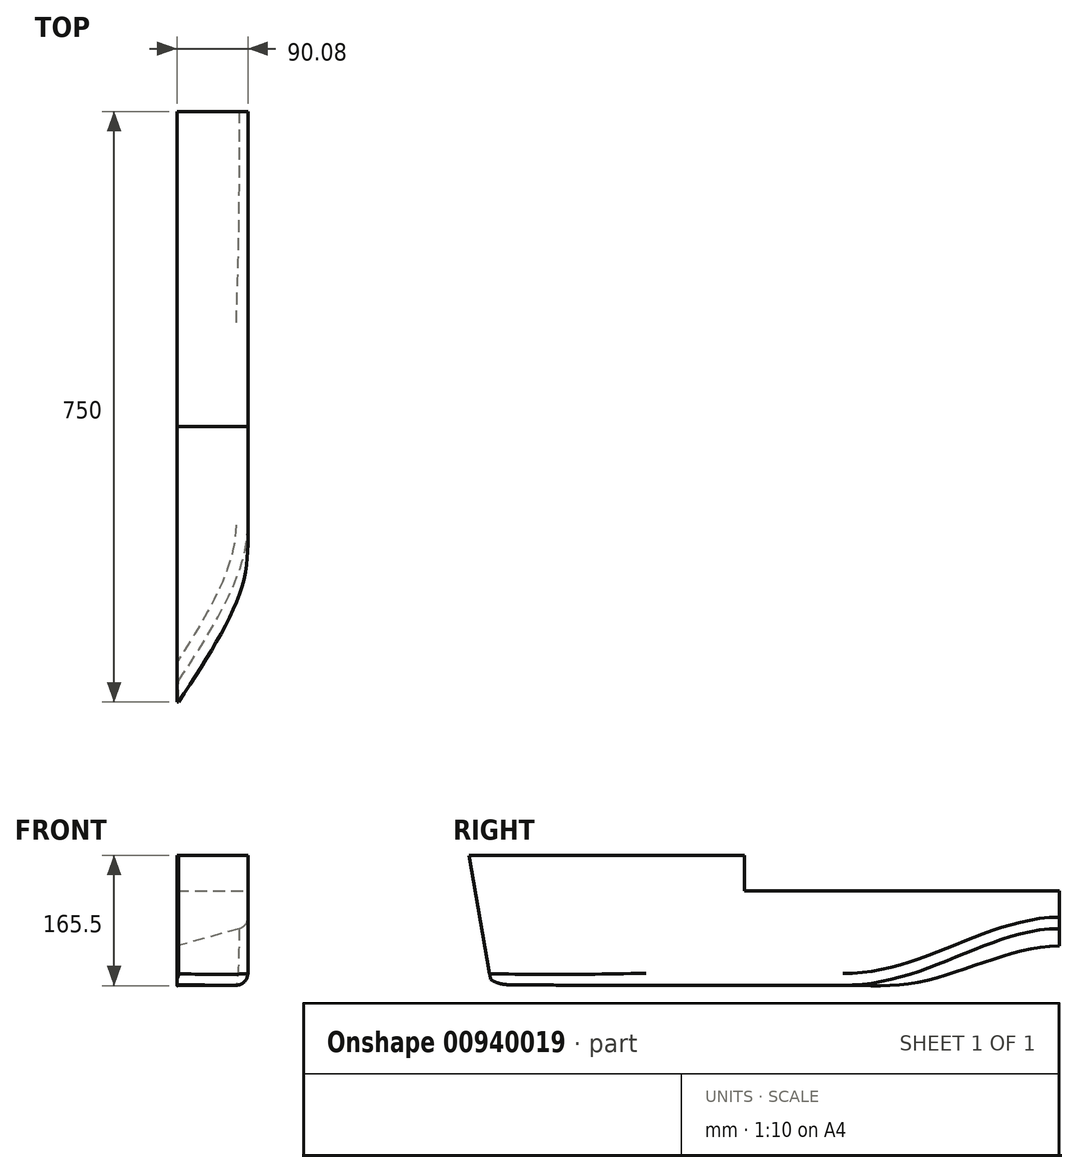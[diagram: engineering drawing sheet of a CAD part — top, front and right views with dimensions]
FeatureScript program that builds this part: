
annotation { "Feature Type Name" : "Feature", "Feature Type Description" : "" }
export const myFeature = defineFeature(function(context is Context, id is Id, definition is map)
    precondition{}
    {
        {
            var Q0;
            Q0=qCreatedBy(makeId("Front.planeOp"),FACE);
            var sketch = newSketch(context, id + "F0", { "sketchPlane" : qUnion([Q0])});
            skLineSegment(sketch, "E0", {"start": v(0, 0) * mm, "end": v(0, 90) * mm});
            skLineSegment(sketch, "E1", {"start": v(0, 90) * mm, "end": v(90, 90) * mm});
            skLineSegment(sketch, "E2", {"start": v(90, 90) * mm, "end": v(90, -75) * mm});
            skLineSegment(sketch, "E3", {"start": v(90, -75) * mm, "end": v(0, -75) * mm});
            skLineSegment(sketch, "E4", {"start": v(0, -75) * mm, "end": v(0, 0) * mm});
            skSolve(sketch);
        }
        {
            var Q0;
            Q0=makeQuery(id+"F0.imprint","IMPRINT",FACE,{"disambiguationData":[TD([[makeQuery(id+"F0.imprint","IMPRINT",EDGE,{"derivedFrom":sQuery(id+"F0.wireOp",EDGE,"E0")}),-1.0]])]});
            extrude(context, id + "F1", {"entities" : qUnion([Q0]), "depth" : 250 * mm, "offsetDistance" : 25 * mm, "symmetric" : true});
        }
        {
            var Q0;
            Q0=makeQuery(id+"F1.opExtrude","SWEPT_FACE",FACE,{"disambiguationData":[OSD([sQuery(id+"F0.wireOp",EDGE,"E0"),sQuery(id+"F0.wireOp",EDGE,"E4")])]});
            var sketch = newSketch(context, id + "F2", { "sketchPlane" : qUnion([Q0])});
            skLineSegment(sketch, "E5", {"start": v(0, 90) * mm, "end": v(350, 90) * mm});
            skLineSegment(sketch, "E6", {"start": v(0, 90) * mm, "end": v(-400, 90) * mm});
            skLineSegment(sketch, "E7", {"start": v(0, -75) * mm, "end": v(-400, -75) * mm});
            skLineSegment(sketch, "E8", {"start": v(0, -75) * mm, "end": v(350, -75) * mm});
            skSolve(sketch);
        }
        {
            var Q0;
            Q0=qCreatedBy(makeId("Front.planeOp"),FACE);
            cPlane(context, id + "F3", {"entities" : qUnion([Q0]), "cplaneType" : CPlaneType.OFFSET, "offset" : 350 * mm, "width" : 150 * mm, "height" : 150 * mm});
        }
        {
            var Q0;
            Q0=qCreatedBy(id+"F3.planeOp",FACE);
            var sketch = newSketch(context, id + "F4", { "sketchPlane" : qUnion([Q0])});
            skLineSegment(sketch, "E9", {"start": v(0, 90) * mm, "end": v(90, 90) * mm});
            skSolve(sketch);
        }
        {
            var Q0;
            Q0=sQuery(id+"F4.wireOp",EDGE,"E9");
            cPlane(context, id + "F5", {"entities" : qUnion([Q0]), "cplaneType" : CPlaneType.LINE_ANGLE, "offset" : 25 * mm, "angle" : 10 * degree, "width" : 150 * mm, "height" : 150 * mm});
        }
        {
            var Q0;
            Q0=qCreatedBy(id+"F5.planeOp",FACE);
            var sketch = newSketch(context, id + "F6", { "sketchPlane" : qUnion([Q0])});
            skLineSegment(sketch, "E10", {"start": v(0, 58.2) * mm, "end": v(0, 149.4) * mm});
            skLineSegment(sketch, "E11", {"start": v(0, 58.2) * mm, "end": v(0, -17.18) * mm});
            skLineSegment(sketch, "E12", {"start": v(0, 149.4) * mm, "end": v(-2, 149.4) * mm});
            skLineSegment(sketch, "E13", {"start": v(-2, 149.4) * mm, "end": v(-2, -17.18) * mm});
            skLineSegment(sketch, "E14", {"start": v(-2, -17.18) * mm, "end": v(0, -17.18) * mm});
            skSolve(sketch);
        }
        {
            var Q0;
            Q0=qCreatedBy(makeId("Front.planeOp"),FACE);
            cPlane(context, id + "F7", {"entities" : qUnion([Q0]), "cplaneType" : CPlaneType.OFFSET, "offset" : 195 * mm, "width" : 150 * mm, "height" : 150 * mm});
        }
        {
            var Q0;
            Q0=qCreatedBy(id+"F7.planeOp",FACE);
            var sketch = newSketch(context, id + "F8", { "sketchPlane" : qUnion([Q0])});
            skLineSegment(sketch, "E15", {"start": v(0, 0) * mm, "end": v(0, 90) * mm});
            skLineSegment(sketch, "E16", {"start": v(0, 90) * mm, "end": v(85, 90) * mm});
            skLineSegment(sketch, "E17", {"start": v(85, 90) * mm, "end": v(73.8, -75) * mm});
            skLineSegment(sketch, "E18", {"start": v(73.8, -75) * mm, "end": v(0, -75) * mm});
            skLineSegment(sketch, "E19", {"start": v(0, -75) * mm, "end": v(0, 0) * mm});
            skSolve(sketch);
        }
        {
            var Q0;
            Q0=qCreatedBy(makeId("Front.planeOp"),FACE);
            cPlane(context, id + "F9", {"entities" : qUnion([Q0]), "cplaneType" : CPlaneType.OFFSET, "offset" : 400 * mm, "oppositeDirection" : true, "width" : 150 * mm, "height" : 150 * mm});
        }
        {
            var Q0;
            Q0=qCreatedBy(id+"F9.planeOp",FACE);
            var sketch = newSketch(context, id + "F10", { "sketchPlane" : qUnion([Q0])});
            skLineSegment(sketch, "E20", {"start": v(0, 0) * mm, "end": v(0, 90) * mm});
            skLineSegment(sketch, "E21", {"start": v(0, 90) * mm, "end": v(90, 90) * mm});
            skLineSegment(sketch, "E22", {"start": v(90, 90) * mm, "end": v(90, 0) * mm});
            skLineSegment(sketch, "E23", {"start": v(90, 0) * mm, "end": v(0, -25) * mm});
            skLineSegment(sketch, "E24", {"start": v(0, -25) * mm, "end": v(0, 0) * mm});
            skSolve(sketch);
        }
        {
            var Q0;
            Q0=qCreatedBy(makeId("Front.planeOp"),FACE);
            cPlane(context, id + "F11", {"entities" : qUnion([Q0]), "cplaneType" : CPlaneType.OFFSET, "offset" : 210 * mm, "oppositeDirection" : true, "width" : 150 * mm, "height" : 150 * mm});
        }
        {
            var Q0;
            Q0=qCreatedBy(id+"F11.planeOp",FACE);
            var sketch = newSketch(context, id + "F12", { "sketchPlane" : qUnion([Q0])});
            skLineSegment(sketch, "E25", {"start": v(0, 0) * mm, "end": v(0, 90) * mm});
            skLineSegment(sketch, "E26", {"start": v(0, 90) * mm, "end": v(90, 90) * mm});
            skLineSegment(sketch, "E27", {"start": v(90, 90) * mm, "end": v(90, -59.23) * mm});
            skLineSegment(sketch, "E28", {"start": v(90, -59.23) * mm, "end": v(0, -73) * mm});
            skLineSegment(sketch, "E29", {"start": v(0, -73) * mm, "end": v(0, 0) * mm});
            skSolve(sketch);
        }
        {
            var Q1;
            Q1=makeQuery(id+"F1.opExtrude","CAP_FACE",FACE,{"disambiguationData":[OSD([sQuery(id+"F0.wireOp",EDGE,"E0"),sQuery(id+"F0.wireOp",EDGE,"E1"),sQuery(id+"F0.wireOp",EDGE,"E2"),sQuery(id+"F0.wireOp",EDGE,"E3"),sQuery(id+"F0.wireOp",EDGE,"E4")])],"isStart":false});
            var Q2;
            Q2=makeQuery(id+"F8.imprint","IMPRINT",FACE,{"disambiguationData":[TD([[makeQuery(id+"F8.imprint","IMPRINT",EDGE,{"derivedFrom":sQuery(id+"F8.wireOp",EDGE,"E15")}),-1.0]])]});
            var Q3;
            Q3=makeQuery(id+"F6.imprint","IMPRINT",FACE,{"disambiguationData":[TD([[makeQuery(id+"F6.imprint","IMPRINT",EDGE,{"derivedFrom":sQuery(id+"F6.wireOp",EDGE,"E10")}),1.0]])]});
            loft(context, id + "F13", {"operationType" : NewBodyOperationType.ADD, "startCondition" : LoftEndDerivativeType.NORMAL_TO_PROFILE, "startMagnitude" : 1, "sheetProfilesArray" : [{ "sheetProfileEntities" : qUnion([Q1]) }, { "sheetProfileEntities" : qUnion([Q2]) }, { "sheetProfileEntities" : qUnion([Q3]) }]});
        }
        {
            var Q1;
            Q1=makeQuery(id+"F1.opExtrude","CAP_FACE",FACE,{"disambiguationData":[OSD([sQuery(id+"F0.wireOp",EDGE,"E0"),sQuery(id+"F0.wireOp",EDGE,"E1"),sQuery(id+"F0.wireOp",EDGE,"E2"),sQuery(id+"F0.wireOp",EDGE,"E3"),sQuery(id+"F0.wireOp",EDGE,"E4")])],"isStart":true});
            var Q2;
            Q2=makeQuery(id+"F12.imprint","IMPRINT",FACE,{"disambiguationData":[TD([[makeQuery(id+"F12.imprint","IMPRINT",EDGE,{"derivedFrom":sQuery(id+"F12.wireOp",EDGE,"E25")}),-1.0]])]});
            var Q3;
            Q3=makeQuery(id+"F10.imprint","IMPRINT",FACE,{"disambiguationData":[TD([[makeQuery(id+"F10.imprint","IMPRINT",EDGE,{"derivedFrom":sQuery(id+"F10.wireOp",EDGE,"E20")}),-1.0]])]});
            var Q4;
            Q4=makeQuery(id+"F1.opExtrude","CAP_VERTEX",VERTEX,{"disambiguationData":[OSD([sQuery(id+"F0.wireOp",EDGE,"E3"),sQuery(id+"F0.wireOp",EDGE,"E4")])],"isStart":true});
            var Q5;
            Q5=sQuery(id+"F12.wireOp",VERTEX,"E28.end");
            var Q6;
            Q6=sQuery(id+"F10.wireOp",VERTEX,"E23.end");
            loft(context, id + "F14", {"operationType" : NewBodyOperationType.ADD, "startCondition" : LoftEndDerivativeType.NORMAL_TO_PROFILE, "startMagnitude" : 1, "endCondition" : LoftEndDerivativeType.NORMAL_TO_PROFILE, "endMagnitude" : 1, "sheetProfilesArray" : [{ "sheetProfileEntities" : qUnion([Q1]) }, { "sheetProfileEntities" : qUnion([Q2]) }, { "sheetProfileEntities" : qUnion([Q3]) }], "matchConnections" : true, "connections" : [{ "connectionEntities" : qUnion([Q4, Q5, Q6]), "connectionEdgeQueries" : qUnion([]), "connectionEdgeParameters" : [] }]});
        }
        {
            var Q0;
            {var subQ0=sQuery(id+"F0.wireOp",EDGE,"E2");Q0=makeQuery(id+"F14.boolean.opBoolean","MERGE",FACE,{"derivedFrom":[makeQuery(id+"F1.opExtrude","SWEPT_FACE",FACE,{"disambiguationData":[OSD([subQ0])]}),makeQuery(id+"F14.opLoft","SWEPT_FACE",FACE,{"disambiguationData":[OSD([sQuery(id+"F0.wireOp",EDGE,"E1"),subQ0,sQuery(id+"F0.wireOp",EDGE,"E3"),sQuery(id+"F10.wireOp",EDGE,"E21"),sQuery(id+"F10.wireOp",EDGE,"E22"),sQuery(id+"F10.wireOp",EDGE,"E23"),sQuery(id+"F12.wireOp",EDGE,"E26"),sQuery(id+"F12.wireOp",EDGE,"E27"),sQuery(id+"F12.wireOp",EDGE,"E28")])]})]});}
            var sketch = newSketch(context, id + "F15", { "sketchPlane" : qUnion([Q0])});
            skLineSegment(sketch, "E30.bottom", {"start": v(0, 90) * mm, "end": v(400, 90) * mm});
            skLineSegment(sketch, "E30.top", {"start": v(0, 45) * mm, "end": v(400, 45) * mm});
            skLineSegment(sketch, "E30.left", {"start": v(0, 90) * mm, "end": v(0, 45) * mm});
            skLineSegment(sketch, "E30.right", {"start": v(400, 90) * mm, "end": v(400, 45) * mm});
            skSolve(sketch);
        }
        {
            var Q0;
            Q0=makeQuery(id+"F15.imprint","IMPRINT",FACE,{"disambiguationData":[TD([[makeQuery(id+"F15.imprint","IMPRINT",EDGE,{"derivedFrom":sQuery(id+"F15.wireOp",EDGE,"E30.top")}),1.0]])]});
            extrude(context, id + "F16", {"entities" : qUnion([Q0]), "operationType" : NewBodyOperationType.REMOVE, "oppositeDirection" : true, "depth" : 90 * mm, "offsetDistance" : 25 * mm});
        }
        {
            var Q0;
            Q0=makeQuery(id+"F13.opLoft","SWEPT_EDGE",EDGE,{"disambiguationData":[OSD([sQuery(id+"F0.wireOp",EDGE,"E2"),sQuery(id+"F0.wireOp",EDGE,"E3"),sQuery(id+"F6.wireOp",EDGE,"E13"),sQuery(id+"F6.wireOp",EDGE,"E14"),sQuery(id+"F8.wireOp",EDGE,"E17"),sQuery(id+"F8.wireOp",EDGE,"E18")])]});
            var Q1;
            Q1=makeQuery(id+"F1.opExtrude","SWEPT_EDGE",EDGE,{"disambiguationData":[OSD([sQuery(id+"F0.wireOp",EDGE,"E2"),sQuery(id+"F0.wireOp",EDGE,"E3")])]});
            fillet(context, id + "F17", {"entities" : qUnion([Q0, Q1]), "radius" : 15 * mm, "tangentPropagation" : true, "allowEdgeOverflow" : false});
        }
    });
